# Revit family: Cleanroom_Pass-Through_TerraUni_Standard-Steel-Wall-mount
name_source: partatom
category: Specialty Equipment
units: mm (PartAtom-declared; Revit-internal decimal feet)

## family parameters
Classification Number = 23.40.70.11.11.11.11
Cut with Voids When Loaded = No
Enable Cutting in Views = No
Host = Face
Maintain Annotation Orientation = No
Part Type = Normal
Room Calculation Point = No
Round Connector Dimension = Use Diameter
Shared = No

## types (36) — shared parameters
Assembly Code = E1020700
Construction Details = http://www.arcat.com
Default Elevation = 4' - 0"
Door Style = NonFireRated-Door : Windowed Door 1 Handle
Include Rack System = Yes
Include ULPA Air Shower = Yes
Keynote = 13 20 00
Manufacturer = Terra Universal, Inc.
Manufacturer Fax = 714-992-2179
Manufacturer Website = http://www.terrauniversal.com
Model_Rack System = Not Applicable
Product Data = http://www.arcat.com
Revision = R1_3_2012
Sales Information = http://www.terrauniversal.com
Send Message = http://www.arcat.com Universal, Inc.&coid=43448&rep=147&fax=714-992-2179&mf=
Specification = http://www.arcat.com
URL = http://www.terrauniversal.com
zero-valued in all types: Expected Lifespan (Years), Maintenance Schedule (Months), Warranty Duration (Years)

## per-type parameters (varying)
| type | Description | Fixture Material | Model | Opening Height | Opening Width | Overall Height | Overall Width | Unit Depth | Unit Height | Unit Width |
| 12x12x12 Electropolished 304 SS | Terra Universal 1992-01C Stainless Steel Pass-Through Chamber | Metal - TerraUniversal - Electropolished 304 SS | 1992-01C | 1' - 0 1/2" | 1' - 0 1/2" | 1' - 2 1/2" | 1' - 2 1/2" | 1' - 0" | 1' - 0" | 1' - 0" |
| 12x12x24 Electropolished 304 SS | Terra Universal Stainless Steel Pass-Through Chamber | Metal - TerraUniversal - Electropolished 304 SS | As Specified | 2' - 0 1/2" | 1' - 0 1/2" | 2' - 2 1/2" | 1' - 2 1/2" | 1' - 0" | 2' - 0" | 1' - 0" |
| 18x18x16 Electropolished 304 SS | Terra Universal Stainless Steel Pass-Through Chamber | Metal - TerraUniversal - Electropolished 304 SS | As Specified | 1' - 4 1/2" | 1' - 6 1/2" | 1' - 6 1/2" | 1' - 8 1/2" | 1' - 6" | 1' - 4" | 1' - 6" |
| 18x18x24 Electropolished 304 SS | Terra Universal Stainless Steel Pass-Through Chamber | Metal - TerraUniversal - Electropolished 304 SS | As Specified | 2' - 0 1/2" | 1' - 6 1/2" | 2' - 2 1/2" | 1' - 8 1/2" | 1' - 6" | 2' - 0" | 1' - 6" |
| 24x24x16 Electropolished 304 SS | Terra Universal Stainless Steel Pass-Through Chamber | Metal - TerraUniversal - Electropolished 304 SS | As Specified | 1' - 4 1/2" | 2' - 0 1/2" | 1' - 6 1/2" | 2' - 2 1/2" | 2' - 0" | 1' - 4" | 2' - 0" |
| 24x24x24 Electropolished 304 SS | Terra Universal Stainless Steel Pass-Through Chamber | Metal - TerraUniversal - Electropolished 304 SS | As Specified | 2' - 0 1/2" | 2' - 0 1/2" | 2' - 2 1/2" | 2' - 2 1/2" | 2' - 0" | 2' - 0" | 2' - 0" |
| 24x36x24 Electropolished 304 SS | Terra Universal Stainless Steel Pass-Through Chamber | Metal - TerraUniversal - Electropolished 304 SS | As Specified | 2' - 0 1/2" | 2' - 0 1/2" | 2' - 2 1/2" | 2' - 2 1/2" | 3' - 0" | 2' - 0" | 2' - 0" |
| 36x36x24 Electropolished 304 SS | Terra Universal Stainless Steel Pass-Through Chamber | Metal - TerraUniversal - Electropolished 304 SS | As Specified | 2' - 0 1/2" | 3' - 0 1/2" | 2' - 2 1/2" | 3' - 2 1/2" | 3' - 0" | 2' - 0" | 3' - 0" |
| 24x24x36 Electropolished 304 SS | Terra Universal Stainless Steel Pass-Through Chamber | Metal - TerraUniversal - Electropolished 304 SS | As Specified | 3' - 0 1/2" | 2' - 0 1/2" | 3' - 2 1/2" | 2' - 2 1/2" | 2' - 0" | 3' - 0" | 2' - 0" |
| 24x24x48 Electropolished 304 SS | Terra Universal Stainless Steel Pass-Through Chamber | Metal - TerraUniversal - Electropolished 304 SS | As Specified | 4' - 0 1/2" | 2' - 0 1/2" | 4' - 2 1/2" | 2' - 2 1/2" | 2' - 0" | 4' - 0" | 2' - 0" |
| 36x36x36 Electropolished 304 SS | Terra Universal Stainless Steel Pass-Through Chamber | Metal - TerraUniversal - Electropolished 304 SS | As Specified | 3' - 0 1/2" | 3' - 0 1/2" | 3' - 2 1/2" | 3' - 2 1/2" | 3' - 0" | 3' - 0" | 3' - 0" |
| 36x36x48 Electropolished 304 SS | Terra Universal Stainless Steel Pass-Through Chamber | Metal - TerraUniversal - Electropolished 304 SS | As Specified | 4' - 0 1/2" | 3' - 0 1/2" | 4' - 2 1/2" | 3' - 2 1/2" | 3' - 0" | 4' - 0" | 3' - 0" |
| 12x12x12 Regular 304 SS | Terra Universal Stainless Steel Pass-Through Chamber | Metal - TerraUniversal - 304 SS | As Specified | 1' - 0 1/2" | 1' - 0 1/2" | 1' - 2 1/2" | 1' - 2 1/2" | 1' - 0" | 1' - 0" | 1' - 0" |
| 12x12x24 Regular 304 SS | Terra Universal Stainless Steel Pass-Through Chamber | Metal - TerraUniversal - 304 SS | As Specified | 2' - 0 1/2" | 1' - 0 1/2" | 2' - 2 1/2" | 1' - 2 1/2" | 1' - 0" | 2' - 0" | 1' - 0" |
| 18x18x16 Regular 304 SS | Terra Universal Stainless Steel Pass-Through Chamber | Metal - TerraUniversal - 304 SS | As Specified | 1' - 4 1/2" | 1' - 6 1/2" | 1' - 6 1/2" | 1' - 8 1/2" | 1' - 6" | 1' - 4" | 1' - 6" |
| 18x18x24 Regular 304 SS | Terra Universal Stainless Steel Pass-Through Chamber | Metal - TerraUniversal - 304 SS | As Specified | 2' - 0 1/2" | 1' - 6 1/2" | 2' - 2 1/2" | 1' - 8 1/2" | 1' - 6" | 2' - 0" | 1' - 6" |
| 24x24x16 Regular 304 SS | Terra Universal Stainless Steel Pass-Through Chamber | Metal - TerraUniversal - 304 SS | As Specified | 1' - 4 1/2" | 2' - 0 1/2" | 1' - 6 1/2" | 2' - 2 1/2" | 2' - 0" | 1' - 4" | 2' - 0" |
| 24x24x24 Regular 304 SS | Terra Universal Stainless Steel Pass-Through Chamber | Metal - TerraUniversal - 304 SS | As Specified | 2' - 0 1/2" | 2' - 0 1/2" | 2' - 2 1/2" | 2' - 2 1/2" | 2' - 0" | 2' - 0" | 2' - 0" |
| 24x36x24 Regular 304 SS | Terra Universal Stainless Steel Pass-Through Chamber | Metal - TerraUniversal - 304 SS | As Specified | 2' - 0 1/2" | 2' - 0 1/2" | 2' - 2 1/2" | 2' - 2 1/2" | 3' - 0" | 2' - 0" | 2' - 0" |
| 36x36x24 Regular 304 SS | Terra Universal Stainless Steel Pass-Through Chamber | Metal - TerraUniversal - 304 SS | As Specified | 2' - 0 1/2" | 3' - 0 1/2" | 2' - 2 1/2" | 3' - 2 1/2" | 3' - 0" | 2' - 0" | 3' - 0" |
| 24x24x36 Regular 304 SS | Terra Universal Stainless Steel Pass-Through Chamber | Metal - TerraUniversal - 304 SS | As Specified | 3' - 0 1/2" | 2' - 0 1/2" | 3' - 2 1/2" | 2' - 2 1/2" | 2' - 0" | 3' - 0" | 2' - 0" |
| 24x24x48 Regular 304 SS | Terra Universal Stainless Steel Pass-Through Chamber | Metal - TerraUniversal - 304 SS | As Specified | 4' - 0 1/2" | 2' - 0 1/2" | 4' - 2 1/2" | 2' - 2 1/2" | 2' - 0" | 4' - 0" | 2' - 0" |
| 36x36x36 Regular 304 SS | Terra Universal Stainless Steel Pass-Through Chamber | Metal - TerraUniversal - 304 SS | As Specified | 3' - 0 1/2" | 3' - 0 1/2" | 3' - 2 1/2" | 3' - 2 1/2" | 3' - 0" | 3' - 0" | 3' - 0" |
| 36x36x48 Regular 304 SS | Terra Universal Stainless Steel Pass-Through Chamber | Metal - TerraUniversal - 304 SS | As Specified | 4' - 0 1/2" | 3' - 0 1/2" | 4' - 2 1/2" | 3' - 2 1/2" | 3' - 0" | 4' - 0" | 3' - 0" |
| 12x12x12 Powder-Coated | Terra Universal Stainless Steel Pass-Through Chamber | Metal - TerraUniversal - Powder-Coated Steel | As Specified | 1' - 0 1/2" | 1' - 0 1/2" | 1' - 2 1/2" | 1' - 2 1/2" | 1' - 0" | 1' - 0" | 1' - 0" |
| 12x12x24 Powder-Coated | Terra Universal Stainless Steel Pass-Through Chamber | Metal - TerraUniversal - Powder-Coated Steel | As Specified | 2' - 0 1/2" | 1' - 0 1/2" | 2' - 2 1/2" | 1' - 2 1/2" | 1' - 0" | 2' - 0" | 1' - 0" |
| 18x18x16 Powder-Coated | Terra Universal Stainless Steel Pass-Through Chamber | Metal - TerraUniversal - Powder-Coated Steel | As Specified | 1' - 4 1/2" | 1' - 6 1/2" | 1' - 6 1/2" | 1' - 8 1/2" | 1' - 6" | 1' - 4" | 1' - 6" |
| 18x18x24 Powder-Coated | Terra Universal Stainless Steel Pass-Through Chamber | Metal - TerraUniversal - Powder-Coated Steel | As Specified | 2' - 0 1/2" | 1' - 6 1/2" | 2' - 2 1/2" | 1' - 8 1/2" | 1' - 6" | 2' - 0" | 1' - 6" |
| 24x24x16 Powder-Coated | Terra Universal Stainless Steel Pass-Through Chamber | Metal - TerraUniversal - Powder-Coated Steel | As Specified | 1' - 4 1/2" | 2' - 0 1/2" | 1' - 6 1/2" | 2' - 2 1/2" | 2' - 0" | 1' - 4" | 2' - 0" |
| 24x24x24 Powder-Coated | Terra Universal Stainless Steel Pass-Through Chamber | Metal - TerraUniversal - Powder-Coated Steel | As Specified | 2' - 0 1/2" | 2' - 0 1/2" | 2' - 2 1/2" | 2' - 2 1/2" | 2' - 0" | 2' - 0" | 2' - 0" |
| 24x36x24 Powder-Coated | Terra Universal Stainless Steel Pass-Through Chamber | Metal - TerraUniversal - Powder-Coated Steel | As Specified | 2' - 0 1/2" | 2' - 0 1/2" | 2' - 2 1/2" | 2' - 2 1/2" | 3' - 0" | 2' - 0" | 2' - 0" |
| 36x36x24 Powder-Coated | Terra Universal Stainless Steel Pass-Through Chamber | Metal - TerraUniversal - Powder-Coated Steel | As Specified | 2' - 0 1/2" | 3' - 0 1/2" | 2' - 2 1/2" | 3' - 2 1/2" | 3' - 0" | 2' - 0" | 3' - 0" |
| 24x24x36 Powder-Coated | Terra Universal Stainless Steel Pass-Through Chamber | Metal - TerraUniversal - Powder-Coated Steel | As Specified | 3' - 0 1/2" | 2' - 0 1/2" | 3' - 2 1/2" | 2' - 2 1/2" | 2' - 0" | 3' - 0" | 2' - 0" |
| 24x24x48 Powder-Coated | Terra Universal Stainless Steel Pass-Through Chamber | Metal - TerraUniversal - Powder-Coated Steel | As Specified | 4' - 0 1/2" | 2' - 0 1/2" | 4' - 2 1/2" | 2' - 2 1/2" | 2' - 0" | 4' - 0" | 2' - 0" |
| 36x36x36 Powder-Coated | Terra Universal Stainless Steel Pass-Through Chamber | Metal - TerraUniversal - Powder-Coated Steel | As Specified | 3' - 0 1/2" | 3' - 0 1/2" | 3' - 2 1/2" | 3' - 2 1/2" | 3' - 0" | 3' - 0" | 3' - 0" |
| 36x36x48 Powder-Coated | Terra Universal Stainless Steel Pass-Through Chamber | Metal - TerraUniversal - Powder-Coated Steel | As Specified | 4' - 0 1/2" | 3' - 0 1/2" | 4' - 2 1/2" | 3' - 2 1/2" | 3' - 0" | 4' - 0" | 3' - 0" |

## geometry (parser evidence)
native form markers: Blend x4, Sweep x4
no freeform markers — native parametric forms only
